# Revit family: TESK_Насос вертикальный_SVM(T)-15
name_source: partatom
category: Оборудование
units: mm (PartAtom-declared; Revit-internal decimal feet)

## family parameters
Всегда вертикально = Да
Классификация = Насос
На основе рабочей плоскости = Нет
Общий = Нет
При загрузке вырезать с полостями = Нет
Размер круглого соединителя = Использовать диаметр
Тип детали = Вставляется
Точка расчета площади = Нет

## types (26) — shared parameters
ADSK_Версия Revit = 2019
ADSK_Версия семейства = 1.0
ADSK_Диаметр условный = 50 мм
ADSK_Единица измерения = шт.
ADSK_Завод-изготовитель = TESK
ADSK_Классификация нагрузок = Прочее
ADSK_Количество = 1
ADSK_Количество фаз = 3
ADSK_Количество фаз числовое = 3
ADSK_Коэффициент мощности = 1
ADSK_Наименование краткое = Вертикальный многоступенчатый центробежный насос
ADSK_Напряжение = 400 В
URL = www.teskpump.ru
Длина_ВспомЛиния = 30 мм
Материал_1 = TESK_Черный_Условный
Материал_2 = TESK_Нержавеющая сталь
Материал_КорпусДвигателя = TESK_Черный_Ребра_Условный
Таблица_Поиска = TESK_SVM(T)-15
УГО_Длина = 300 мм
Фланец_Толщина = 24 мм

## per-type parameters (varying)
| type | ADSK_Код изделия | ADSK_Масса | ADSK_Масса_Текст | ADSK_Наименование | ADSK_Номинальная мощность | ADSK_Полная мощность | Высота_Корпуса | Высота_Перехода | Двигатель_Высота | Двигатель_ОтступКоробки | Двигатель_Ширина | Материал_КорпусУлитка | Напор максимальный |
| SVM 15-1 1.1kW 3x380V 50Hz IE3 | 7715-1003380NSSF | 33 | 33 | Вертикальный многоступенчатый центробежный насос SVM, DN50, PN25, Hmax=13м (3x380V 50Hz IE3) | 1 кВт | 1 кВ·А | 352 мм | 130 мм | 280 мм | 142 мм | 170 мм | TESK_Нержавеющая сталь | 13 |
| SVM 15-2 2.2kW 3x380V 50Hz IE3 | 7715-20003380NSSF | 42 | 42 | Вертикальный многоступенчатый центробежный насос SVM, DN50, PN25, Hmax=26м (3x380V 50Hz IE3) | 2 кВт | 2 кВ·А | 397 мм | 150 мм | 333 мм | 155 мм | 190 мм | TESK_Нержавеющая сталь | 26 |
| SVM 15-3 3kW 3x380V 50Hz IE3 | 7715-30003380NSSF | 50 | 50 | Вертикальный многоступенчатый центробежный насос SVM, DN50, PN25, Hmax=39.5м (3x380V 50Hz IE3) | 3 кВт | 3 кВ·А | 452 мм | 170 мм | 348 мм | 165 мм | 197 мм | TESK_Нержавеющая сталь | 39.5 |
| SVM 15-4 4kW 3x380V 50Hz IE3 | 7715-40003380NSSF | 59 | 59 | Вертикальный многоступенчатый центробежный насос SVM, DN50, PN25, Hmax=53м (3x380V 50Hz IE3) | 4 кВт | 4 кВ·А | 497 мм | 190 мм | 382 мм | 185 мм | 230 мм | TESK_Нержавеющая сталь | 53 |
| SVM 15-5 4kW 3x380V 50Hz IE3 | 7715-50003380NSSF | 60 | 60 | Вертикальный многоступенчатый центробежный насос SVM, DN50, PN25, Hmax=67м (3x380V 50Hz IE3) | 4 кВт | 4 кВ·А | 542 мм | 190 мм | 382 мм | 185 мм | 230 мм | TESK_Нержавеющая сталь | 67 |
| SVM 15-6 5.5kW 3x380V 50Hz IE3 | 7715-60003380NSSF | 77 | 77 | Вертикальный многоступенчатый центробежный насос SVM, DN50, PN25, Hmax=80.5м (3x380V 50Hz IE3) | 6 кВт | 6 кВ·А | 607 мм | 210 мм | 435 мм | 210 мм | 260 мм | TESK_Нержавеющая сталь | 80.5 |
| SVM 15-7 5.5kW 3x380V 50Hz IE3 | 7715-70003380NSSF | 78 | 78 | Вертикальный многоступенчатый центробежный насос SVM, DN50, PN25, Hmax=94м (3x380V 50Hz IE3) | 6 кВт | 6 кВ·А | 652 мм | 210 мм | 435 мм | 210 мм | 260 мм | TESK_Нержавеющая сталь | 94 |
| SVM 15-8 7.5kW 3x380V 50Hz IE3 | 7715-80003380NSSF | 86 | 86 | Вертикальный многоступенчатый центробежный насос SVM, DN50, PN25, Hmax=107.5м (3x380V 50Hz IE3) | 8 кВт | 8 кВ·А | 697 мм | 210 мм | 435 мм | 210 мм | 260 мм | TESK_Нержавеющая сталь | 107.5 |
| SVM 15-9 7.5kW 3x380V 50Hz IE3 | 7715-90003380NSSF | 87 | 87 | Вертикальный многоступенчатый центробежный насос SVM, DN50, PN25, Hmax=120м (3x380V 50Hz IE3) | 8 кВт | 8 кВ·А | 742 мм | 210 мм | 435 мм | 210 мм | 260 мм | TESK_Нержавеющая сталь | 120 |
| SVM 15-10 11kW 3x380V 50Hz IE3 | 7715-100003380NSSF | 160 | 160 | Вертикальный многоступенчатый центробежный насос SVM, DN50, PN25, Hmax=134м (3x380V 50Hz IE3) | 11 кВт | 11 кВ·А | 875 мм | 230 мм | 580 мм | 260 мм | 350 мм | TESK_Нержавеющая сталь | 134 |
| SVM 15-12 11kW 3x380V 50Hz IE3 | 7715-120003380NSSF | 161 | 161 | Вертикальный многоступенчатый центробежный насос SVM, DN50, PN25, Hmax=161м (3x380V 50Hz IE3) | 11 кВт | 11 кВ·А | 965 мм | 230 мм | 580 мм | 260 мм | 350 мм | TESK_Нержавеющая сталь | 161 |
| SVM 15-14 11kW 3x380V 50Hz IE3 | 7715-140003380NSSF | 162 | 162 | Вертикальный многоступенчатый центробежный насос SVM, DN50, PN25, Hmax=186м (3x380V 50Hz IE3) | 11 кВт | 11 кВ·А | 1055 мм | 230 мм | 580 мм | 260 мм | 350 мм | TESK_Нержавеющая сталь | 186 |
| SVM 15-17 15kW 3x380V 50Hz IE3 | 7715-170003380NSSF | 179 | 179 | Вертикальный многоступенчатый центробежный насос SVM, DN50, PN25, Hmax=227м (3x380V 50Hz IE3) | 15 кВт | 15 кВ·А | 1190 мм | 230 мм | 580 мм | 260 мм | 350 мм | TESK_Нержавеющая сталь | 227 |
| SVMT 15-1 1.1kW 3x380V 50Hz IE3 | 7715-1003380N | 33 | 33 | Вертикальный многоступенчатый центробежный насос SVMT, DN50, PN25, Hmax=13м (3x380V 50Hz IE3) | 1 кВт | 1 кВ·А | 352 мм | 130 мм | 280 мм | 142 мм | 170 мм | TESK_Черный_Условный | 13 |
| SVMT 15-2 2.2kW 3x380V 50Hz IE3 | 7715-20003380N | 42 | 42 | Вертикальный многоступенчатый центробежный насос SVMT, DN50, PN25, Hmax=26м (3x380V 50Hz IE3) | 2 кВт | 2 кВ·А | 397 мм | 150 мм | 333 мм | 155 мм | 190 мм | TESK_Черный_Условный | 26 |
| SVMT 15-3 3kW 3x380V 50Hz IE3 | 7715-30003380N | 50 | 50 | Вертикальный многоступенчатый центробежный насос SVMT, DN50, PN25, Hmax=39.5м (3x380V 50Hz IE3) | 3 кВт | 3 кВ·А | 452 мм | 170 мм | 348 мм | 165 мм | 197 мм | TESK_Черный_Условный | 39.5 |
| SVMT 15-4 4kW 3x380V 50Hz IE3 | 7715-40003380N | 59 | 59 | Вертикальный многоступенчатый центробежный насос SVMT, DN50, PN25, Hmax=53м (3x380V 50Hz IE3) | 4 кВт | 4 кВ·А | 497 мм | 190 мм | 382 мм | 185 мм | 230 мм | TESK_Черный_Условный | 53 |
| SVMT 15-5 4kW 3x380V 50Hz IE3 | 7715-50003380N | 60 | 60 | Вертикальный многоступенчатый центробежный насос SVMT, DN50, PN25, Hmax=67м (3x380V 50Hz IE3) | 4 кВт | 4 кВ·А | 542 мм | 190 мм | 382 мм | 185 мм | 230 мм | TESK_Черный_Условный | 67 |
| SVMT 15-6 5.5kW 3x380V 50Hz IE3 | 7715-60003380N | 77 | 77 | Вертикальный многоступенчатый центробежный насос SVMT, DN50, PN25, Hmax=80.5м (3x380V 50Hz IE3) | 6 кВт | 6 кВ·А | 607 мм | 210 мм | 435 мм | 210 мм | 260 мм | TESK_Черный_Условный | 80.5 |
| SVMT 15-7 5.5kW 3x380V 50Hz IE3 | 7715-70003380N | 78 | 78 | Вертикальный многоступенчатый центробежный насос SVMT, DN50, PN25, Hmax=94м (3x380V 50Hz IE3) | 6 кВт | 6 кВ·А | 652 мм | 210 мм | 435 мм | 210 мм | 260 мм | TESK_Черный_Условный | 94 |
| SVMT 15-8 7.5kW 3x380V 50Hz IE3 | 7715-80003380N | 86 | 86 | Вертикальный многоступенчатый центробежный насос SVMT, DN50, PN25, Hmax=107.5м (3x380V 50Hz IE3) | 8 кВт | 8 кВ·А | 697 мм | 210 мм | 435 мм | 210 мм | 260 мм | TESK_Черный_Условный | 107.5 |
| SVMT 15-9 7.5kW 3x380V 50Hz IE3 | 7715-90003380N | 87 | 87 | Вертикальный многоступенчатый центробежный насос SVMT, DN50, PN25, Hmax=120м (3x380V 50Hz IE3) | 8 кВт | 8 кВ·А | 742 мм | 210 мм | 435 мм | 210 мм | 260 мм | TESK_Черный_Условный | 120 |
| SVMT 15-10 11kW 3x380V 50Hz IE3 | 7715-100003380N | 160 | 160 | Вертикальный многоступенчатый центробежный насос SVMT, DN50, PN25, Hmax=134м (3x380V 50Hz IE3) | 11 кВт | 11 кВ·А | 875 мм | 230 мм | 580 мм | 260 мм | 350 мм | TESK_Черный_Условный | 134 |
| SVMT 15-12 11kW 3x380V 50Hz IE3 | 7715-120003380N | 161 | 161 | Вертикальный многоступенчатый центробежный насос SVMT, DN50, PN25, Hmax=161м (3x380V 50Hz IE3) | 11 кВт | 11 кВ·А | 965 мм | 230 мм | 580 мм | 260 мм | 350 мм | TESK_Черный_Условный | 161 |
| SVMT 15-14 11kW 3x380V 50Hz IE3 | 7715-140003380N | 162 | 162 | Вертикальный многоступенчатый центробежный насос SVMT, DN50, PN25, Hmax=186м (3x380V 50Hz IE3) | 11 кВт | 11 кВ·А | 1055 мм | 230 мм | 580 мм | 260 мм | 350 мм | TESK_Черный_Условный | 186 |
| SVMT 15-17 15kW 3x380V 50Hz IE3 | 7715-170003380N | 179 | 179 | Вертикальный многоступенчатый центробежный насос SVMT, DN50, PN25, Hmax=227м (3x380V 50Hz IE3) | 15 кВт | 15 кВ·А | 1190 мм | 230 мм | 580 мм | 260 мм | 350 мм | TESK_Черный_Условный | 227 |

note: column(s) folded — value = type name in every type: ADSK_Марка
